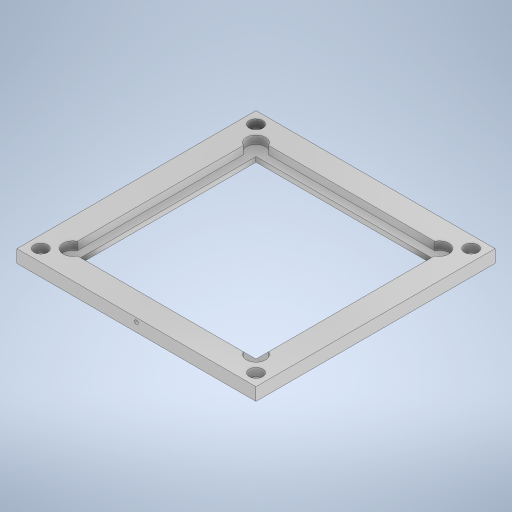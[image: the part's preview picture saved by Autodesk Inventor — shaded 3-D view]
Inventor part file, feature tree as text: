
AUTODESK INVENTOR PART (.ipt)
format: ipt  version: 2023.2 (Build 272271030, 271C)  size: 335,360 bytes
history: native  units: mm
features: sketch x6, extrude x4, hole x2, other x1
ambient origin geometry x8: Origin, YZ Plane, XZ Plane, XY Plane, X Axis, Y Axis, Z Axis, Center Point
bodies: Body1 (feature_tree)
feature tree (13):
  other  "Sólido1"
  extrude  "Extrusão1"  Depth=150.0mm
  extrude  "Extrusão2"  Depth=120.0mm
  extrude  "Extrusão3"  TaperAngle=0.0deg  [1 undecoded]
  extrude  "Extrusão4"  Depth=5.0mm TaperAngle=0.0deg
  hole  "Furo1"  [1 undecoded]
  hole  "Furo2"  [1 undecoded]
  sketch  "Esboço1"  dims[d0=150.0mm d1=150.0mm]
  sketch  "Esboço2"  dims[d2=8.0mm d3=0.0mm d4=120.0mm]
  sketch  "Esboço3"  dims[d5=120.0mm d6=0.0mm]
  sketch  "Esboço4"  dims[d7=0.0mm d8=5.0mm d9=0.0mm]
  sketch  "Esboço5"  dims[d10=110.0mm d11=0.0mm]
  sketch  "Esboço6"  dims[d12=0.0mm d13=3.0mm d14=0.0mm d15=12.0mm d16=2.5mm d17=2.5mm d18=2.5mm d19=2.5mm d20=2.5mm d21=2.5mm d22=2.5mm d23=2.5mm d24=5.0mm d25=0.0mm d26=5.0mm d27=2.5mm d28=0.0mm d29=2.459mm d30=6.0mm d31=4.0mm d32=2.0mm d33=90.0deg d34=8.8mm d35=20.594885mm d36=7.5mm d37=15.0mm d38=7.5mm d39=7.5mm d40=7.5mm d41=7.5mm d42=7.5mm d43=7.5mm d44=7.5mm d45=5.0mm d46=10.0mm d47=8.5mm d48=5.0mm d49=90.0deg d50=8.0mm d51=20.594885mm]
note: 3 required parameter values undecoded (feature->parameter linkage not recoverable at this tier; creation-order binding heuristic only, values carry confidence <= 0.55)
